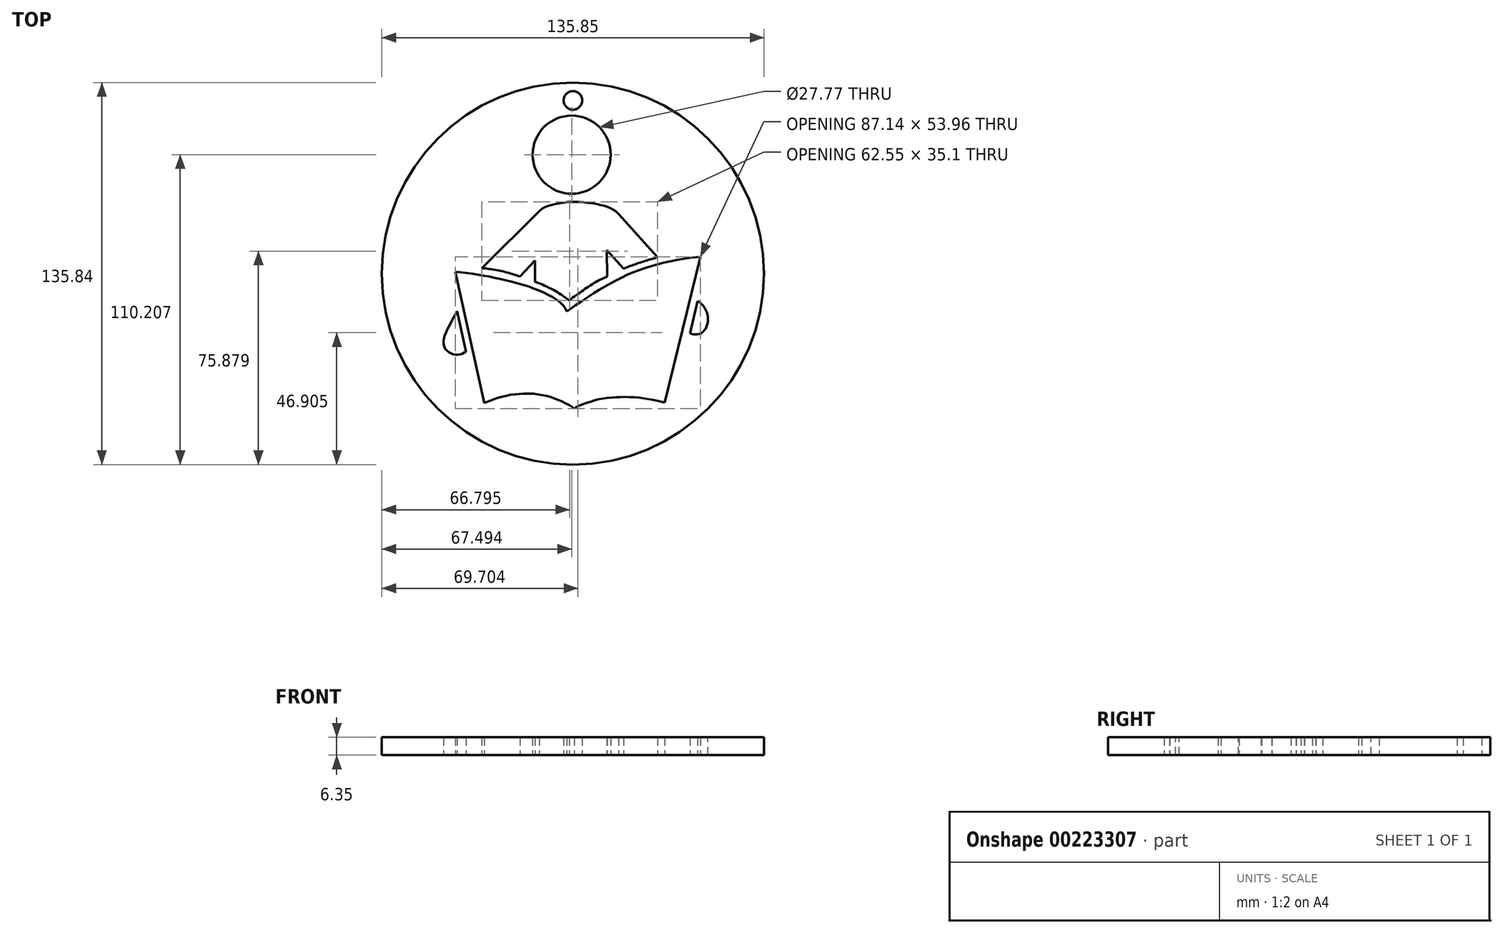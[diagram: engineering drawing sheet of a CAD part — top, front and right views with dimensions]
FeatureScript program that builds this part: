
annotation { "Feature Type Name" : "Feature", "Feature Type Description" : "" }
export const myFeature = defineFeature(function(context is Context, id is Id, definition is map)
    precondition{}
    {
        {
            var Q0;
            Q0=qCreatedBy(makeId("Top.planeOp"),FACE);
            var sketch = newSketch(context, id + "F0", { "sketchPlane" : qUnion([Q0])});
            skLineSegment(sketch, "E0", {"start": v(3.17, -45.9) * mm, "end": v(15.83, 5.96) * mm});
            skFitSpline(sketch, "E1", {"points": [v(15.83, 5.96) * mm, v(13.86, 5.82) * mm, v(9.63, 5.25) * mm, v(4.54, 4.24) * mm, v(-0.46, 3.03) * mm, v(-4.39, 1.75) * mm, v(-8.82, 0.14) * mm, v(-12.66, -1.65) * mm, v(-16.35, -3.54) * mm, v(-20.52, -6) * mm, v(-24.46, -8.55) * mm, v(-29.33, -11.8) * mm, v(-31.63, -13.54) * mm], "startDerivative": vector(-31.52, -1.7) * mm, "endDerivative": vector(-29.64, -23.42) * mm});
            skFitSpline(sketch, "E2", {"points": [v(-31.63, -13.54) * mm, v(-32.04, -12.68) * mm, v(-32.72, -11.64) * mm, v(-33.79, -10.47) * mm, v(-35.6, -9.11) * mm, v(-37.53, -7.9) * mm, v(-39.94, -6.73) * mm, v(-42.66, -5.59) * mm, v(-45.45, -4.56) * mm, v(-48.07, -3.76) * mm, v(-51.66, -2.8) * mm, v(-55.32, -1.92) * mm, v(-58.5, -1.24) * mm, v(-61.64, -0.66) * mm, v(-65.07, -0.11) * mm, v(-68.6, 0.36) * mm, v(-71.3, 0.63) * mm], "startDerivative": vector(-9.82, 22.5) * mm, "endDerivative": vector(-41.1, 3.84) * mm});
            skLineSegment(sketch, "E3", {"start": v(-71.3, 0.63) * mm, "end": v(-60.97, -46.06) * mm});
            skFitSpline(sketch, "E4", {"points": [v(-60.97, -46.06) * mm, v(-59.84, -45.54) * mm, v(-58.13, -44.9) * mm, v(-55.71, -44.1) * mm, v(-52.87, -43.4) * mm, v(-49.83, -42.88) * mm, v(-47.36, -42.75) * mm, v(-43.76, -42.74) * mm, v(-41.29, -43.1) * mm, v(-38.5, -43.62) * mm, v(-36.25, -44.33) * mm, v(-34.1, -45.17) * mm, v(-31.5, -46.45) * mm, v(-29.68, -47.5) * mm, v(-29.05, -48) * mm], "startDerivative": vector(20.63, 9.95) * mm, "endDerivative": vector(12.9, -11.21) * mm});
            skFitSpline(sketch, "E5", {"points": [v(-29.05, -48) * mm, v(-28.05, -47.33) * mm, v(-25.66, -46.34) * mm, v(-22.67, -45.36) * mm, v(-19.56, -44.58) * mm, v(-15.26, -44.08) * mm, v(-12.15, -43.91) * mm, v(-7.67, -44) * mm, v(-4.09, -44.43) * mm, v(-0.46, -45.04) * mm, v(1.44, -45.45) * mm, v(3.17, -45.9) * mm], "startDerivative": vector(15.07, 11.27) * mm, "endDerivative": vector(24.56, -6.76) * mm});
            skCircle(sketch, "E6", {"center": v(-29.95, 42.29) * mm, "radius": 13.88 * mm});
            skPoint(sketch, "E6.first.point", {"position": v(-30.03, 28.4) * mm});
            skPoint(sketch, "E6.second.point", {"position": v(-29.83, 56.17) * mm});
            skPoint(sketch, "E6.third.point", {"position": v(-17.2, 47.8) * mm});
            skLineSegment(sketch, "E7", {"start": v(12.1, -21.3) * mm, "end": v(14.73, -9.8) * mm});
            skFitSpline(sketch, "E8", {"points": [v(12.1, -21.3) * mm, v(13.07, -21.54) * mm, v(13.97, -21.58) * mm, v(15.65, -21.4) * mm, v(16.84, -20.52) * mm, v(17.62, -19.63) * mm, v(18.2, -18.24) * mm, v(18.5, -16.58) * mm, v(18.25, -14.43) * mm, v(17.55, -12.56) * mm, v(16.55, -11.17) * mm, v(15.68, -10.36) * mm, v(14.73, -9.8) * mm], "startDerivative": vector(14.42, -4.3) * mm, "endDerivative": vector(-13.4, 7.25) * mm});
            skLineSegment(sketch, "E9", {"start": v(-70.62, -13.32) * mm, "end": v(-67.54, -27.8) * mm});
            skFitSpline(sketch, "E10", {"points": [v(-67.54, -27.8) * mm, v(-68.53, -28.31) * mm, v(-69.9, -28.83) * mm, v(-71.8, -28.75) * mm, v(-73.34, -28.16) * mm, v(-74.88, -26.77) * mm, v(-75.45, -24.98) * mm, v(-75.3, -22.84) * mm, v(-74.16, -19.88) * mm, v(-72.64, -17.02) * mm, v(-70.62, -13.32) * mm], "startDerivative": vector(-13.4, -7.08) * mm, "endDerivative": vector(15.13, 27.8) * mm});
            skLineSegment(sketch, "E11", {"start": v(-48.3, -1.1) * mm, "end": v(-42.95, 4.66) * mm});
            skLineSegment(sketch, "E12", {"start": v(-42.95, 4.66) * mm, "end": v(-42.95, -2.95) * mm});
            skFitSpline(sketch, "E13", {"points": [v(-42.95, -2.95) * mm, v(-41.1, -3.64) * mm, v(-38.5, -4.8) * mm, v(-36.47, -5.8) * mm, v(-33.87, -7.37) * mm, v(-32.33, -8.46) * mm, v(-30.77, -9.59) * mm], "startDerivative": vector(11.31, -3.97) * mm, "endDerivative": vector(10.54, -7.52) * mm});
            skFitSpline(sketch, "E14", {"points": [v(-30.77, -9.59) * mm, v(-29.64, -8.59) * mm, v(-27.04, -6.77) * mm, v(-24.35, -4.9) * mm, v(-21.28, -2.95) * mm, v(-18.68, -1.63) * mm, v(-17.3, -1.06) * mm], "startDerivative": vector(7.76, 7.5) * mm, "endDerivative": vector(10.92, 4.23) * mm});
            skLineSegment(sketch, "E15", {"start": v(-17.3, -1.06) * mm, "end": v(-17.5, 8.42) * mm});
            skLineSegment(sketch, "E16", {"start": v(-17.5, 8.42) * mm, "end": v(-11.48, 1.78) * mm});
            skFitSpline(sketch, "E17", {"points": [v(-11.48, 1.78) * mm, v(-8.73, 2.83) * mm, v(-3.74, 4.52) * mm, v(0.63, 5.79) * mm], "startDerivative": vector(8.97, 3.56) * mm, "endDerivative": vector(12.1, 3.37) * mm});
            skLineSegment(sketch, "E18", {"start": v(0.63, 5.79) * mm, "end": v(-13.33, 21.15) * mm});
            skFitSpline(sketch, "E19", {"points": [v(-13.33, 21.15) * mm, v(-14.3, 22.22) * mm, v(-17, 23.58) * mm, v(-21.34, 24.76) * mm, v(-27.72, 25.49) * mm, v(-32.66, 25.29) * mm, v(-38.58, 23.96) * mm, v(-41.52, 22.26) * mm], "startDerivative": vector(-9.5, 12.97) * mm, "endDerivative": vector(-28.9, -23.84) * mm});
            skLineSegment(sketch, "E20", {"start": v(-41.52, 22.26) * mm, "end": v(-61.92, 1.92) * mm});
            skFitSpline(sketch, "E21", {"points": [v(-48.3, -1.1) * mm, v(-50.01, -0.47) * mm, v(-52.5, 0.3) * mm, v(-55, 0.9) * mm, v(-58.27, 1.5) * mm, v(-60.54, 1.83) * mm, v(-61.92, 1.92) * mm], "startDerivative": vector(-10.09, 3.76) * mm, "endDerivative": vector(-11.21, 0.43) * mm});
            skSolve(sketch);
        }
        {
            var Q0;
            Q0=qCreatedBy(makeId("Top.planeOp"),FACE);
            var sketch = newSketch(context, id + "F1", { "sketchPlane" : qUnion([Q0])});
            skCircle(sketch, "E22", {"center": v(-29.52, 0) * mm, "radius": 67.92 * mm});
            skCircle(sketch, "E23", {"center": v(-29.52, 61.59) * mm, "radius": 3.3 * mm});
            skSolve(sketch);
        }
        {
            var Q0;
            Q0=makeQuery(id+"F1.imprint","IMPRINT",FACE,{"disambiguationData":[TD([[makeQuery(id+"F1.imprint","IMPRINT",EDGE,{"derivedFrom":sQuery(id+"F1.wireOp",EDGE,"E22")}),1.0]])]});
            extrude(context, id + "F2", {"entities" : qUnion([Q0]), "depth" : 6.35 * mm});
        }
        {
            var Q0;
            Q0 = qSketchRegion(id + "F0", true);
            extrude(context, id + "F3", {"entities" : qUnion([Q0]), "operationType" : NewBodyOperationType.REMOVE, "depth" : 6.35 * mm});
        }
    });
